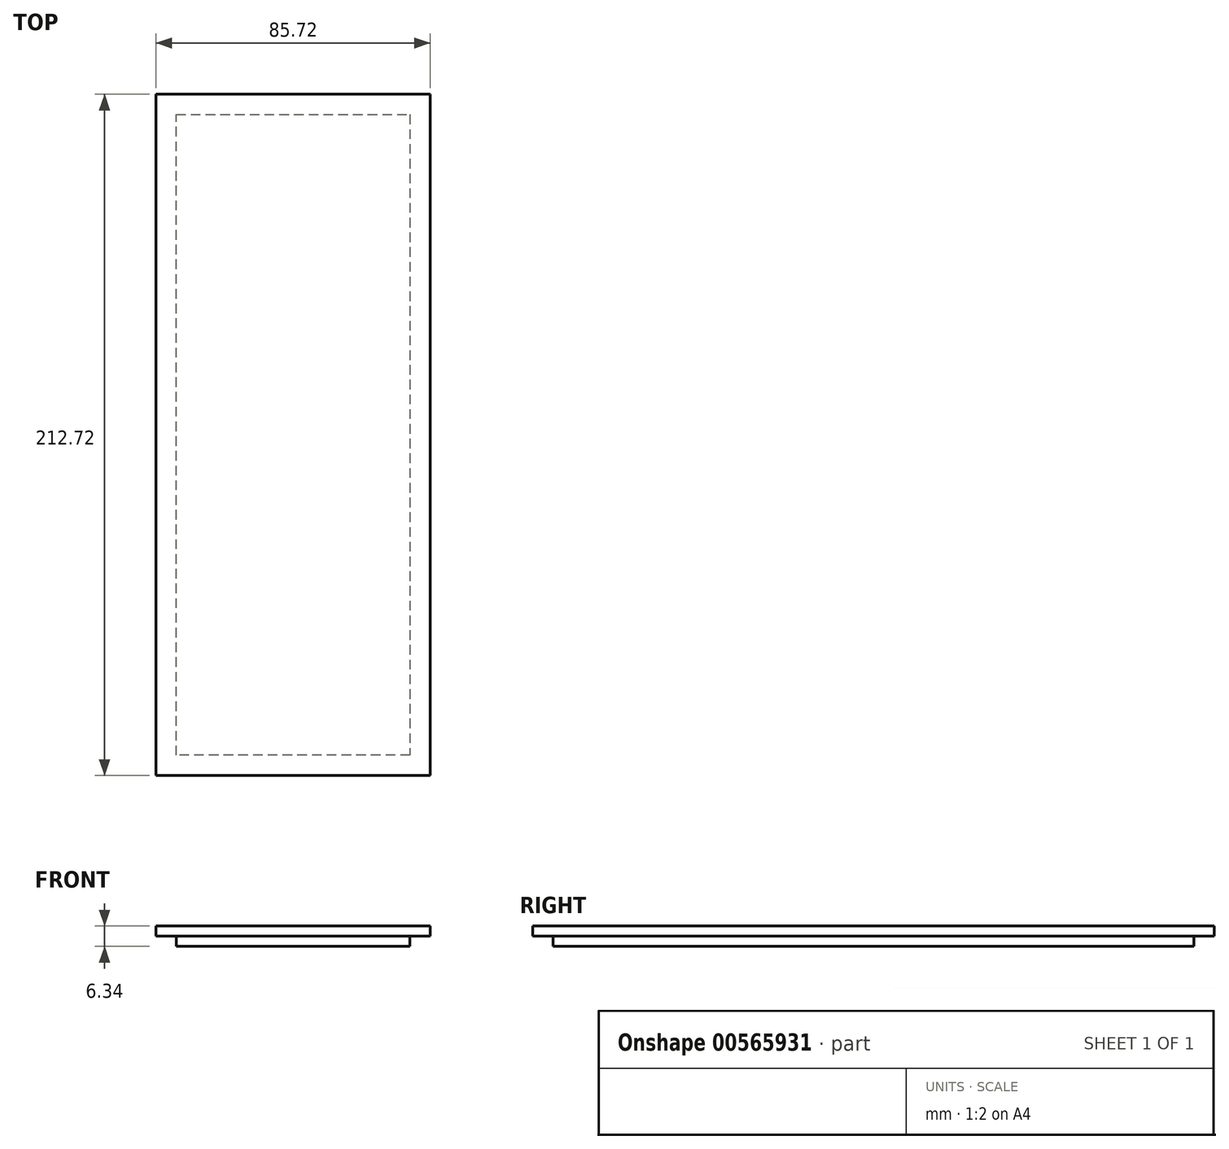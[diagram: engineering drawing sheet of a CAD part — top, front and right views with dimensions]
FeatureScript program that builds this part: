
annotation { "Feature Type Name" : "Feature", "Feature Type Description" : "" }
export const myFeature = defineFeature(function(context is Context, id is Id, definition is map)
    precondition{}
    {
        {
            var Q0;
            Q0=qCreatedBy(makeId("Top.planeOp"),FACE);
            var sketch = newSketch(context, id + "F0", { "sketchPlane" : qUnion([Q0])});
            skLineSegment(sketch, "E0.bottom", {"start": v(-42.86, 106.36) * mm, "end": v(42.86, 106.36) * mm});
            skLineSegment(sketch, "E0.top", {"start": v(-42.86, -106.36) * mm, "end": v(42.86, -106.36) * mm});
            skLineSegment(sketch, "E0.left", {"start": v(-42.86, 106.36) * mm, "end": v(-42.86, -106.36) * mm});
            skLineSegment(sketch, "E0.right", {"start": v(42.86, 106.36) * mm, "end": v(42.86, -106.36) * mm});
            skLineSegment(sketch, "E1", {"start": v(-42.86, 106.36) * mm, "end": v(42.86, -106.36) * mm, "construction": true});
            skSolve(sketch);
        }
        {
            var Q0;
            Q0 = qSketchRegion(id + "F0", true);
            extrude(context, id + "F1", {"entities" : qUnion([Q0]), "endBound" : BoundingType.SYMMETRIC, "depth" : 6.35 * mm, "offsetDistance" : 25.4 * mm});
        }
        {
            var Q0;
            Q0=makeQuery(id+"F1.opExtrude","CAP_FACE",FACE,{"disambiguationData":[OSD([sQuery(id+"F0.wireOp",EDGE,"E0.bottom"),sQuery(id+"F0.wireOp",EDGE,"E0.top"),sQuery(id+"F0.wireOp",EDGE,"E0.left"),sQuery(id+"F0.wireOp",EDGE,"E0.right")])],"isStart":true});
            var sketch = newSketch(context, id + "F2", { "sketchPlane" : qUnion([Q0])});
            skLineSegment(sketch, "E2.1", {"start": v(42.86, -106.36) * mm, "end": v(42.86, 106.36) * mm});
            skLineSegment(sketch, "E3.0", {"start": v(-42.86, 106.36) * mm, "end": v(42.86, 106.36) * mm});
            skLineSegment(sketch, "E4.0", {"start": v(-42.86, -106.36) * mm, "end": v(-42.86, 106.36) * mm});
            skLineSegment(sketch, "E5.0", {"start": v(-42.86, -106.36) * mm, "end": v(42.86, -106.36) * mm});
            skLineSegment(sketch, "E6.0", {"start": v(-36.51, 100.01) * mm, "end": v(-36.51, -100.01) * mm});
            skLineSegment(sketch, "E6.1", {"start": v(36.51, 100.01) * mm, "end": v(-36.51, 100.01) * mm});
            skLineSegment(sketch, "E6.2", {"start": v(36.51, -100.01) * mm, "end": v(36.51, 100.01) * mm});
            skLineSegment(sketch, "E6.3", {"start": v(-36.51, -100.01) * mm, "end": v(36.51, -100.01) * mm});
            skSolve(sketch);
        }
        {
            var Q0;
            Q0 = qSketchRegion(id + "F2", true);
            extrude(context, id + "F3", {"entities" : qUnion([Q0]), "operationType" : NewBodyOperationType.REMOVE, "oppositeDirection" : true, "depth" : 3.17 * mm, "offsetDistance" : 25.4 * mm});
        }
    });
